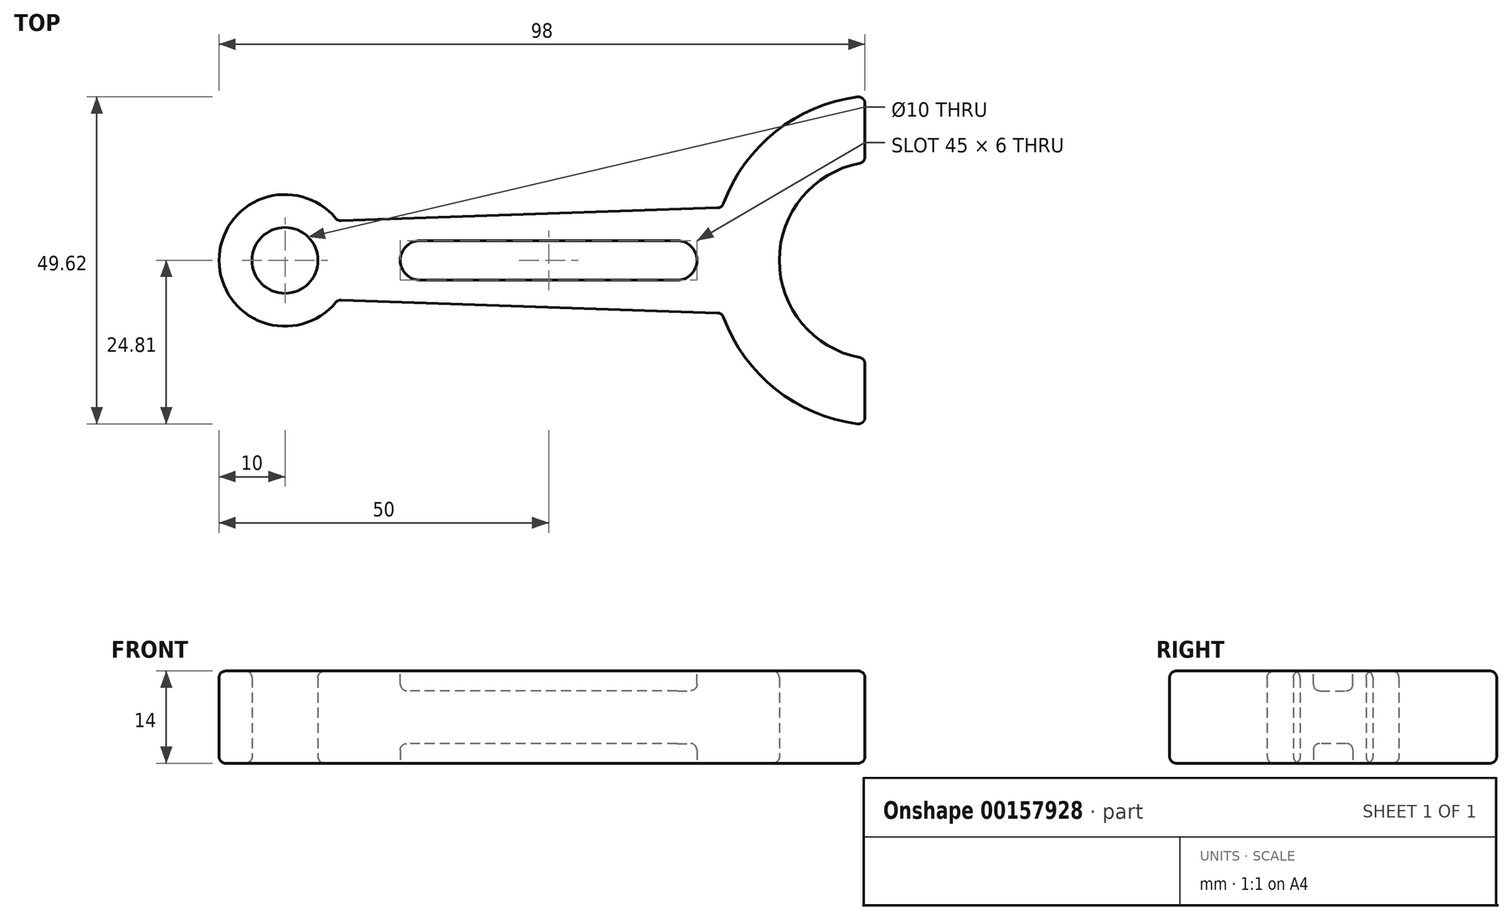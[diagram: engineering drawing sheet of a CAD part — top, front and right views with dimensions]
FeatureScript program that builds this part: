
annotation { "Feature Type Name" : "Feature", "Feature Type Description" : "" }
export const myFeature = defineFeature(function(context is Context, id is Id, definition is map)
    precondition{}
    {
        {
            var Q0;
            Q0=qCreatedBy(makeId("Top.planeOp"),FACE);
            var sketch = newSketch(context, id + "F0", { "sketchPlane" : qUnion([Q0])});
            skCircle(sketch, "E0", {"center": v(0, 0) * mm, "radius": 5 * mm});
            skArc(sketch, "E1", {"start": v(8, 6) * mm, "mid": v(-10, 0) * mm, "end": v(8, -6) * mm});
            skArc(sketch, "E2", {"start": v(88, 14.87) * mm, "mid": v(75, 0) * mm, "end": v(88, -14.87) * mm});
            skArc(sketch, "E3", {"start": v(88, 24.92) * mm, "mid": v(74.62, 19.71) * mm, "end": v(66.31, 8) * mm});
            skLineSegment(sketch, "E4", {"start": v(8, 6) * mm, "end": v(66.31, 8) * mm});
            skLineSegment(sketch, "E5", {"start": v(90, 0) * mm, "end": v(0, 0) * mm, "construction": true});
            skLineSegment(sketch, "E6", {"start": v(88, 14.87) * mm, "end": v(88, 24.92) * mm});
            skLineSegment(sketch, "E7", {"start": v(88, -24.92) * mm, "end": v(88, -14.87) * mm});
            skLineSegment(sketch, "E8.MirrorCS", {"start": v(8, -6) * mm, "end": v(66.31, -8) * mm});
            skArc(sketch, "E9.trimOffspring", {"start": v(66.31, -8) * mm, "mid": v(74.62, -19.71) * mm, "end": v(88, -24.92) * mm});
            skSolve(sketch);
        }
        {
            var Q0;
            Q0=makeQuery(id+"F0.imprint","IMPRINT",FACE,{"disambiguationData":[TD([[makeQuery(id+"F0.imprint","IMPRINT",EDGE,{"derivedFrom":sQuery(id+"F0.wireOp",EDGE,"E0")}),-1.0]])]});
            extrude(context, id + "F1", {"entities" : qUnion([Q0]), "depth" : 7 * mm});
        }
        {
            var Q0;
            Q0=makeQuery(id+"F1.opExtrude","CAP_FACE",FACE,{"disambiguationData":[OSD([sQuery(id+"F0.wireOp",EDGE,"E0"),sQuery(id+"F0.wireOp",EDGE,"E1"),sQuery(id+"F0.wireOp",EDGE,"E2"),sQuery(id+"F0.wireOp",EDGE,"E3"),sQuery(id+"F0.wireOp",EDGE,"E4"),sQuery(id+"F0.wireOp",EDGE,"E6"),sQuery(id+"F0.wireOp",EDGE,"E7"),sQuery(id+"F0.wireOp",EDGE,"E8.MirrorCS"),sQuery(id+"F0.wireOp",EDGE,"E9.trimOffspring")])],"isStart":true});
            var sketch = newSketch(context, id + "F2", { "sketchPlane" : qUnion([Q0])});
            skCircle(sketch, "E10.0", {"center": v(0, 0) * mm, "radius": 5 * mm});
            skArc(sketch, "E11.0", {"start": v(88, -14.87) * mm, "mid": v(75, 0) * mm, "end": v(88, 14.87) * mm});
            skLineSegment(sketch, "E12", {"start": v(90, 0) * mm, "end": v(0, 0) * mm, "construction": true});
            skLineSegment(sketch, "E13.bottom", {"start": v(59.5, 3) * mm, "end": v(20.5, 3) * mm});
            skLineSegment(sketch, "E13.top", {"start": v(59.5, -3) * mm, "end": v(20.5, -3) * mm});
            skLineSegment(sketch, "E13.left", {"start": v(62.5, 0) * mm, "end": v(62.5, 0) * mm});
            skLineSegment(sketch, "E13.right", {"start": v(17.5, 0) * mm, "end": v(17.5, 0) * mm});
            skPoint(sketch, "E13.middle", {"position": v(40, 0) * mm});
            skPoint(sketch, "E14.visualSharp", {"position": v(17.5, 3) * mm});
            skArc(sketch, "E14.filletArc", {"start": v(20.5, 3) * mm, "mid": v(18.38, 2.12) * mm, "end": v(17.5, 0) * mm});
            skPoint(sketch, "E15.visualSharp", {"position": v(62.5, 3) * mm});
            skArc(sketch, "E15.filletArc", {"start": v(62.5, 0) * mm, "mid": v(61.62, 2.12) * mm, "end": v(59.5, 3) * mm});
            skPoint(sketch, "E16.visualSharp", {"position": v(62.5, -3) * mm});
            skArc(sketch, "E16.filletArc", {"start": v(59.5, -3) * mm, "mid": v(61.62, -2.12) * mm, "end": v(62.5, 0) * mm});
            skPoint(sketch, "E17.visualSharp", {"position": v(17.5, -3) * mm});
            skArc(sketch, "E17.filletArc", {"start": v(17.5, 0) * mm, "mid": v(18.38, -2.12) * mm, "end": v(20.5, -3) * mm});
            skSolve(sketch);
        }
        {
            var Q0;
            Q0 = qSketchRegion(id + "F2", true);
            extrude(context, id + "F3", {"entities" : qUnion([Q0]), "operationType" : NewBodyOperationType.REMOVE, "oppositeDirection" : true, "depth" : 3 * mm});
        }
        {
            var Q0;
            Q0=makeQuery(id+"F1.opExtrude","CAP_EDGE",EDGE,{"disambiguationData":[OSD([sQuery(id+"F0.wireOp",EDGE,"E1")])],"isStart":true});
            var Q1;
            Q1=makeQuery(id+"F1.opExtrude","CAP_EDGE",EDGE,{"disambiguationData":[OSD([sQuery(id+"F0.wireOp",EDGE,"E3")])],"isStart":true});
            var Q2;
            Q2=makeQuery(id+"F1.opExtrude","CAP_EDGE",EDGE,{"disambiguationData":[OSD([sQuery(id+"F0.wireOp",EDGE,"E9.trimOffspring")])],"isStart":true});
            var Q3;
            Q3=makeQuery(id+"F1.opExtrude","CAP_EDGE",EDGE,{"disambiguationData":[OSD([sQuery(id+"F0.wireOp",EDGE,"E8.MirrorCS")])],"isStart":true});
            var Q4;
            Q4=makeQuery(id+"F1.opExtrude","CAP_EDGE",EDGE,{"disambiguationData":[OSD([sQuery(id+"F0.wireOp",EDGE,"E0")])],"isStart":true});
            var Q5;
            Q5=makeQuery(id+"F1.opExtrude","CAP_EDGE",EDGE,{"disambiguationData":[OSD([sQuery(id+"F0.wireOp",EDGE,"E2")])],"isStart":true});
            var Q6;
            Q6=makeQuery(id+"F1.opExtrude","CAP_EDGE",EDGE,{"disambiguationData":[OSD([sQuery(id+"F0.wireOp",EDGE,"E4")])],"isStart":true});
            var Q7;
            Q7=makeQuery(id+"F3.boolean.opBoolean","COPY",EDGE,{"derivedFrom":makeQuery(id+"F3.opExtrude","CAP_EDGE",EDGE,{"disambiguationData":[OSD([sQuery(id+"F2.wireOp",EDGE,"E13.top")])],"isStart":true})});
            var Q8;
            Q8=makeQuery(id+"F3.boolean.opBoolean","COPY",EDGE,{"derivedFrom":makeQuery(id+"F3.opExtrude","CAP_EDGE",EDGE,{"disambiguationData":[OSD([sQuery(id+"F2.wireOp",EDGE,"E13.bottom")])],"isStart":false})});
            var Q9;
            Q9=makeQuery(id+"F3.boolean.opBoolean","COPY",EDGE,{"derivedFrom":makeQuery(id+"F3.opExtrude","CAP_EDGE",EDGE,{"disambiguationData":[OSD([sQuery(id+"F2.wireOp",EDGE,"E13.bottom")])],"isStart":true})});
            var Q10;
            Q10=makeQuery(id+"F3.boolean.opBoolean","COPY",EDGE,{"derivedFrom":makeQuery(id+"F3.opExtrude","CAP_EDGE",EDGE,{"disambiguationData":[OSD([sQuery(id+"F2.wireOp",EDGE,"E14.filletArc"),sQuery(id+"F2.wireOp",EDGE,"E17.filletArc")])],"isStart":true})});
            var Q11;
            Q11=makeQuery(id+"F1.opExtrude","CAP_EDGE",EDGE,{"disambiguationData":[OSD([sQuery(id+"F0.wireOp",EDGE,"E6")])],"isStart":true});
            var Q12;
            Q12=makeQuery(id+"F1.opExtrude","SWEPT_EDGE",EDGE,{"disambiguationData":[OSD([sQuery(id+"F0.wireOp",EDGE,"E3"),sQuery(id+"F0.wireOp",EDGE,"E4")])]});
            var Q13;
            Q13=makeQuery(id+"F1.opExtrude","SWEPT_EDGE",EDGE,{"disambiguationData":[OSD([sQuery(id+"F0.wireOp",EDGE,"E1"),sQuery(id+"F0.wireOp",EDGE,"E4")])]});
            var Q14;
            Q14=makeQuery(id+"F1.opExtrude","SWEPT_EDGE",EDGE,{"disambiguationData":[OSD([sQuery(id+"F0.wireOp",EDGE,"E8.MirrorCS"),sQuery(id+"F0.wireOp",EDGE,"E9.trimOffspring")])]});
            var Q15;
            Q15=makeQuery(id+"F1.opExtrude","SWEPT_EDGE",EDGE,{"disambiguationData":[OSD([sQuery(id+"F0.wireOp",EDGE,"E2"),sQuery(id+"F0.wireOp",EDGE,"E6")])]});
            var Q16;
            Q16=makeQuery(id+"F1.opExtrude","SWEPT_EDGE",EDGE,{"disambiguationData":[OSD([sQuery(id+"F0.wireOp",EDGE,"E3"),sQuery(id+"F0.wireOp",EDGE,"E6")])]});
            var Q17;
            Q17=makeQuery(id+"F1.opExtrude","CAP_EDGE",EDGE,{"disambiguationData":[OSD([sQuery(id+"F0.wireOp",EDGE,"E7")])],"isStart":true});
            var Q18;
            Q18=makeQuery(id+"F1.opExtrude","SWEPT_EDGE",EDGE,{"disambiguationData":[OSD([sQuery(id+"F0.wireOp",EDGE,"E2"),sQuery(id+"F0.wireOp",EDGE,"E7")])]});
            var Q19;
            Q19=makeQuery(id+"F1.opExtrude","SWEPT_EDGE",EDGE,{"disambiguationData":[OSD([sQuery(id+"F0.wireOp",EDGE,"E1"),sQuery(id+"F0.wireOp",EDGE,"E8.MirrorCS")])]});
            var Q20;
            Q20=makeQuery(id+"F1.opExtrude","SWEPT_EDGE",EDGE,{"disambiguationData":[OSD([sQuery(id+"F0.wireOp",EDGE,"E7"),sQuery(id+"F0.wireOp",EDGE,"E9.trimOffspring")])]});
            var Q21;
            Q21=makeQuery(id+"F3.boolean.opBoolean","COPY",EDGE,{"derivedFrom":makeQuery(id+"F3.opExtrude","SWEPT_EDGE",EDGE,{"disambiguationData":[OSD([sQuery(id+"F2.wireOp",EDGE,"E13.top"),sQuery(id+"F2.wireOp",EDGE,"E17.filletArc")])]})});
            var Q22;
            Q22=makeQuery(id+"F3.boolean.opBoolean","COPY",EDGE,{"derivedFrom":makeQuery(id+"F3.opExtrude","SWEPT_EDGE",EDGE,{"disambiguationData":[OSD([sQuery(id+"F2.wireOp",EDGE,"E13.bottom"),sQuery(id+"F2.wireOp",EDGE,"E14.filletArc")])]})});
            var Q23;
            Q23=makeQuery(id+"F3.boolean.opBoolean","COPY",EDGE,{"derivedFrom":makeQuery(id+"F3.opExtrude","CAP_EDGE",EDGE,{"disambiguationData":[OSD([sQuery(id+"F2.wireOp",EDGE,"E14.filletArc"),sQuery(id+"F2.wireOp",EDGE,"E17.filletArc")])],"isStart":false})});
            var Q24;
            Q24=makeQuery(id+"F3.boolean.opBoolean","COPY",EDGE,{"derivedFrom":makeQuery(id+"F3.opExtrude","CAP_EDGE",EDGE,{"disambiguationData":[OSD([sQuery(id+"F2.wireOp",EDGE,"E13.top")])],"isStart":false})});
            var Q25;
            Q25=makeQuery(id+"F3.boolean.opBoolean","COPY",EDGE,{"derivedFrom":makeQuery(id+"F3.opExtrude","CAP_EDGE",EDGE,{"disambiguationData":[OSD([sQuery(id+"F2.wireOp",EDGE,"E15.filletArc"),sQuery(id+"F2.wireOp",EDGE,"E16.filletArc")])],"isStart":true})});
            var Q26;
            Q26=makeQuery(id+"F3.boolean.opBoolean","COPY",EDGE,{"derivedFrom":makeQuery(id+"F3.opExtrude","SWEPT_EDGE",EDGE,{"disambiguationData":[OSD([sQuery(id+"F2.wireOp",EDGE,"E13.top"),sQuery(id+"F2.wireOp",EDGE,"E16.filletArc")])]})});
            var Q27;
            Q27=makeQuery(id+"F3.boolean.opBoolean","COPY",EDGE,{"derivedFrom":makeQuery(id+"F3.opExtrude","CAP_EDGE",EDGE,{"disambiguationData":[OSD([sQuery(id+"F2.wireOp",EDGE,"E15.filletArc"),sQuery(id+"F2.wireOp",EDGE,"E16.filletArc")])],"isStart":false})});
            var Q28;
            Q28=makeQuery(id+"F3.boolean.opBoolean","COPY",EDGE,{"derivedFrom":makeQuery(id+"F3.opExtrude","SWEPT_EDGE",EDGE,{"disambiguationData":[OSD([sQuery(id+"F2.wireOp",EDGE,"E13.bottom"),sQuery(id+"F2.wireOp",EDGE,"E15.filletArc")])]})});
            fillet(context, id + "F4", {"entities" : qUnion([Q0, Q1, Q2, Q3, Q4, Q5, Q6, Q7, Q8, Q9, Q10, Q11, Q12, Q13, Q14, Q15, Q16, Q17, Q18, Q19, Q20, Q21, Q22, Q23, Q24, Q25, Q26, Q27, Q28]), "radius" : 1 * mm, "tangentPropagation" : true, "allowEdgeOverflow" : false});
        }
        {
            var Q0;
            Q0=makeQuery(id+"F1.opExtrude","SWEPT_BODY",BODY,{"disambiguationData":[OSD([sQuery(id+"F0.wireOp",EDGE,"E0"),sQuery(id+"F0.wireOp",EDGE,"E1"),sQuery(id+"F0.wireOp",EDGE,"E2"),sQuery(id+"F0.wireOp",EDGE,"E3"),sQuery(id+"F0.wireOp",EDGE,"E4"),sQuery(id+"F0.wireOp",EDGE,"E6"),sQuery(id+"F0.wireOp",EDGE,"E7"),sQuery(id+"F0.wireOp",EDGE,"E8.MirrorCS"),sQuery(id+"F0.wireOp",EDGE,"E9.trimOffspring")])]});
            var Q1;
            Q1=makeQuery(id+"F1.opExtrude","CAP_FACE",FACE,{"disambiguationData":[OSD([sQuery(id+"F0.wireOp",EDGE,"E0"),sQuery(id+"F0.wireOp",EDGE,"E1"),sQuery(id+"F0.wireOp",EDGE,"E2"),sQuery(id+"F0.wireOp",EDGE,"E3"),sQuery(id+"F0.wireOp",EDGE,"E4"),sQuery(id+"F0.wireOp",EDGE,"E6"),sQuery(id+"F0.wireOp",EDGE,"E7"),sQuery(id+"F0.wireOp",EDGE,"E8.MirrorCS"),sQuery(id+"F0.wireOp",EDGE,"E9.trimOffspring")])],"isStart":false});
            mirror(context, id + "F5", {"operationType" : NewBodyOperationType.ADD, "entities" : qUnion([Q0]), "mirrorPlane" : qUnion([Q1])});
        }
    });
